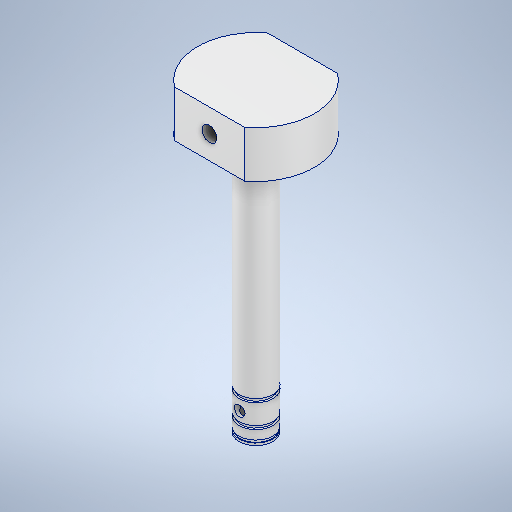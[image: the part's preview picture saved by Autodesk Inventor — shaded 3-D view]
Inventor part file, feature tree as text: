
AUTODESK INVENTOR PART (.ipt)
format: ipt  version: 2025 (Build 290162000, 162)  size: 384,512 bytes
history: native  units: in
note: dims shown in document units (in); Inventor stores cm internally (conversion verified against a paired STEP export)
features: sketch x8, hole x4, extrude x3, revolve x1
ambient origin geometry x8: Origin, YZ Plane, XZ Plane, XY Plane, X Axis, Y Axis, Z Axis, Center Point
bodies: Solid1 (feature_tree)
feature tree (16):
  extrude  "Extrusion1"  Depth=4.3602in TaperAngle=0.0deg
  extrude  "Extrusion2"  Depth=0.7874in TaperAngle=0.0deg
  extrude  "Extrusion3"  Depth=0.7874in
  hole  "Hole4"  [1 undecoded]
  hole  "Hole3"  [1 undecoded]
  hole  "Hole5"  [1 undecoded]
  hole  "Hole6"  [1 undecoded]
  revolve  "Revolution1"  [1 undecoded]
  sketch  "Sketch1"  dims[d0=0.5748in d1=4.3602in d2=0.0in]
  sketch  "Sketch3"  dims[d12=1.9685in d13=0.7874in d14=0.0in]
  sketch  "Sketch5"  dims[d24=0.7874in d25=0.7874in]
  sketch  "Sketch6"  dims[d26=0.0in d27=0.0in d28=0.7874in]
  sketch  "Sketch7"  dims[d29=0.3937in]
  sketch  "Sketch8"  dims[d30=0.234in d31=0.2711in d32=0.0246in d33=0.2346in d34=0.1575in d35=0.0787in d36=90.0deg d37=0.6102in d38=0.8108in d39=0.1476in]
  sketch  "Sketch9"  dims[d40=0.1476in]
  sketch  "Sketch11"  dims[d41=0.1772in d42=0.2711in d43=0.1575in d44=0.0787in d45=90.0deg d46=4.7539in d47=0.8108in d48=0.7874in d49=0.3937in d50=0.234in d51=0.2341in d52=0.0246in d53=0.236in d54=0.1575in d55=0.0787in d56=90.0deg d57=0.6102in d58=0.8108in d59=0.4528in d60=0.1772in d61=0.2341in d62=0.1575in d63=0.0787in d64=90.0deg d65=0.6102in d66=0.8108in d77=360.0deg d78=0.0315in d79=0.0591in d80=0.6299in d81=0.0315in d82=0.0591in d83=0.2362in d84=0.0138in d85=0.0433in d86=0.0394in]
note: 5 required parameter values undecoded (feature->parameter linkage not recoverable at this tier; creation-order binding heuristic only, values carry confidence <= 0.55)